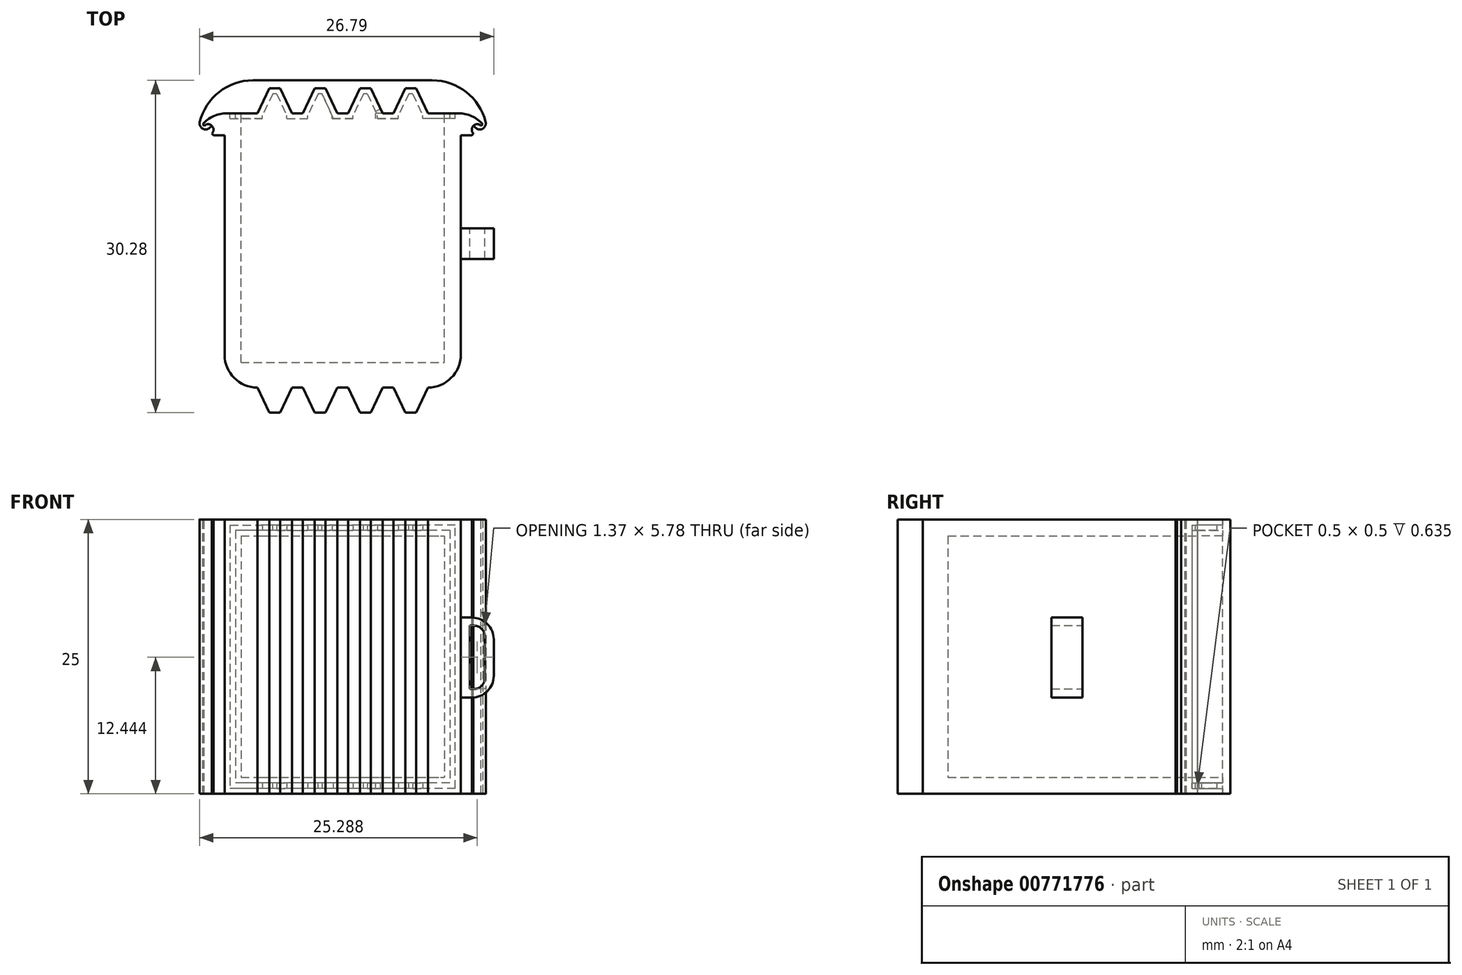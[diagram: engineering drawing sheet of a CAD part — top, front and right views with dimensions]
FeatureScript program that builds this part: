
annotation { "Feature Type Name" : "Feature", "Feature Type Description" : "" }
export const myFeature = defineFeature(function(context is Context, id is Id, definition is map)
    precondition{}
    {
        {
            var Q0;
            Q0=qCreatedBy(makeId("Top.planeOp"),FACE);
            var sketch = newSketch(context, id + "F0", { "sketchPlane" : qUnion([Q0])});
            skLineSegment(sketch, "E0", {"start": v(-21.99, 0) * mm, "end": v(-21.99, 25) * mm});
            skLineSegment(sketch, "E1", {"start": v(-21.99, 25) * mm, "end": v(-18.99, 25) * mm});
            skLineSegment(sketch, "E2", {"start": v(-18.99, 25) * mm, "end": v(-17.92, 27.28) * mm});
            skLineSegment(sketch, "E3", {"start": v(-17.92, 27.28) * mm, "end": v(-16.92, 27.28) * mm});
            skLineSegment(sketch, "E4", {"start": v(-16.92, 27.28) * mm, "end": v(-15.86, 25) * mm});
            skLineSegment(sketch, "E5", {"start": v(-15.86, 25) * mm, "end": v(-14.86, 25) * mm});
            skLineSegment(sketch, "E6", {"start": v(-14.86, 25) * mm, "end": v(-13.8, 27.28) * mm});
            skLineSegment(sketch, "E7", {"start": v(-13.8, 27.28) * mm, "end": v(-12.8, 27.28) * mm});
            skLineSegment(sketch, "E8", {"start": v(-12.8, 27.28) * mm, "end": v(-11.73, 25) * mm});
            skLineSegment(sketch, "E9", {"start": v(-11.73, 25) * mm, "end": v(-10.73, 25) * mm});
            skLineSegment(sketch, "E10", {"start": v(-10.73, 25) * mm, "end": v(-9.67, 27.28) * mm});
            skLineSegment(sketch, "E11", {"start": v(-9.67, 27.28) * mm, "end": v(-8.67, 27.28) * mm});
            skLineSegment(sketch, "E12", {"start": v(-8.67, 27.28) * mm, "end": v(-7.6, 25) * mm});
            skLineSegment(sketch, "E13", {"start": v(-7.6, 25) * mm, "end": v(-6.6, 25) * mm});
            skLineSegment(sketch, "E14", {"start": v(-6.6, 25) * mm, "end": v(-5.54, 27.28) * mm});
            skLineSegment(sketch, "E15", {"start": v(-5.54, 27.28) * mm, "end": v(-4.54, 27.28) * mm});
            skLineSegment(sketch, "E16", {"start": v(-4.54, 27.28) * mm, "end": v(-3.47, 25) * mm});
            skLineSegment(sketch, "E17", {"start": v(-3.47, 25) * mm, "end": v(-0.47, 25) * mm});
            skLineSegment(sketch, "E18", {"start": v(-0.47, 25) * mm, "end": v(-0.47, 0) * mm});
            skLineSegment(sketch, "E19", {"start": v(-33.17, 12.5) * mm, "end": v(42.68, 12.5) * mm, "construction": true});
            skLineSegment(sketch, "E20.MirrorCS", {"start": v(-13.8, -2.28) * mm, "end": v(-12.8, -2.28) * mm});
            skLineSegment(sketch, "E21.MirrorCS", {"start": v(-9.67, -2.28) * mm, "end": v(-8.67, -2.28) * mm});
            skLineSegment(sketch, "E22.MirrorCS", {"start": v(-7.6, 0) * mm, "end": v(-6.6, 0) * mm});
            skLineSegment(sketch, "E23.MirrorCS", {"start": v(-15.86, 0) * mm, "end": v(-14.86, 0) * mm});
            skLineSegment(sketch, "E24.MirrorCS", {"start": v(-5.54, -2.28) * mm, "end": v(-4.54, -2.28) * mm});
            skLineSegment(sketch, "E25.MirrorCS", {"start": v(-21.99, 0) * mm, "end": v(-18.99, 0) * mm});
            skLineSegment(sketch, "E26.MirrorCS", {"start": v(-14.86, 0) * mm, "end": v(-13.8, -2.28) * mm});
            skLineSegment(sketch, "E27.MirrorCS", {"start": v(-4.54, -2.28) * mm, "end": v(-3.47, 0) * mm});
            skLineSegment(sketch, "E28.MirrorCS", {"start": v(-10.73, 0) * mm, "end": v(-9.67, -2.28) * mm});
            skLineSegment(sketch, "E29.MirrorCS", {"start": v(-18.99, 0) * mm, "end": v(-17.92, -2.28) * mm});
            skLineSegment(sketch, "E30.MirrorCS", {"start": v(-11.73, 0) * mm, "end": v(-10.73, 0) * mm});
            skLineSegment(sketch, "E31.MirrorCS", {"start": v(-3.47, 0) * mm, "end": v(-0.47, 0) * mm});
            skLineSegment(sketch, "E32.MirrorCS", {"start": v(-16.92, -2.28) * mm, "end": v(-15.86, 0) * mm});
            skLineSegment(sketch, "E33.MirrorCS", {"start": v(-17.92, -2.28) * mm, "end": v(-16.92, -2.28) * mm});
            skLineSegment(sketch, "E34.MirrorCS", {"start": v(-12.8, -2.28) * mm, "end": v(-11.73, 0) * mm});
            skLineSegment(sketch, "E35.MirrorCS", {"start": v(-6.6, 0) * mm, "end": v(-5.54, -2.28) * mm});
            skLineSegment(sketch, "E36.MirrorCS", {"start": v(-8.67, -2.28) * mm, "end": v(-7.6, 0) * mm});
            skSolve(sketch);
        }
        {
            var Q0;
            Q0=makeQuery(id+"F0.imprint","IMPRINT",FACE,{"disambiguationData":[TD([[makeQuery(id+"F0.imprint","IMPRINT",EDGE,{"derivedFrom":sQuery(id+"F0.wireOp",EDGE,"E0")}),-1.0]])]});
            extrude(context, id + "F1", {"entities" : qUnion([Q0]), "depth" : 25 * mm, "offsetDistance" : 25 * mm});
        }
        {
            var Q0;
            Q0=makeQuery(id+"F1.opExtrude","SWEPT_FACE",FACE,{"disambiguationData":[OSD([sQuery(id+"F0.wireOp",EDGE,"E15")])]});
            var sketch = newSketch(context, id + "F2", { "sketchPlane" : qUnion([Q0])});
            skLineSegment(sketch, "E37.0", {"start": v(20.49, 23.5) * mm, "end": v(20.49, 1.5) * mm});
            skLineSegment(sketch, "E38", {"start": v(20.49, 1.5) * mm, "end": v(1.97, 1.5) * mm});
            skLineSegment(sketch, "E39.0", {"start": v(1.97, 23.5) * mm, "end": v(1.97, 1.5) * mm});
            skLineSegment(sketch, "E40", {"start": v(20.49, 23.5) * mm, "end": v(1.97, 23.5) * mm});
            skPoint(sketch, "E41.start.orphan", {"position": v(24.34, 0) * mm});
            skSolve(sketch);
        }
        {
            var Q0;
            Q0 = qSketchRegion(id + "F2", true);
            extrude(context, id + "F3", {"entities" : qUnion([Q0]), "operationType" : NewBodyOperationType.REMOVE, "oppositeDirection" : true, "depth" : 25 * mm, "offsetDistance" : 25 * mm});
        }
        {
            var Q0;
            Q0=makeQuery(id+"F1.opExtrude","SWEPT_FACE",FACE,{"disambiguationData":[OSD([sQuery(id+"F0.wireOp",EDGE,"E1")])]});
            var sketch = newSketch(context, id + "F4", { "sketchPlane" : qUnion([Q0])});
            skLineSegment(sketch, "E42", {"start": v(-1.53, 0) * mm, "end": v(-1.53, 25) * mm});
            skLineSegment(sketch, "E43", {"start": v(23.99, 0) * mm, "end": v(23.99, 25) * mm});
            skLineSegment(sketch, "E44", {"start": v(23.99, 25) * mm, "end": v(21.99, 25) * mm});
            skLineSegment(sketch, "E45", {"start": v(23.99, 0) * mm, "end": v(21.99, 0) * mm});
            skLineSegment(sketch, "E46.0", {"start": v(0.47, 25) * mm, "end": v(0.47, 0) * mm});
            skLineSegment(sketch, "E47.0", {"start": v(21.99, 25) * mm, "end": v(21.99, 0) * mm});
            skLineSegment(sketch, "E48.trimOffspring", {"start": v(0.47, 0) * mm, "end": v(-1.53, 0) * mm});
            skLineSegment(sketch, "E49.trimOffspring", {"start": v(0.47, 25) * mm, "end": v(-1.53, 25) * mm});
            skSolve(sketch);
        }
        {
            var Q0;
            Q0=makeQuery(id+"F4.imprint","IMPRINT",FACE,{"disambiguationData":[TD([[makeQuery(id+"F4.imprint","IMPRINT",EDGE,{"derivedFrom":sQuery(id+"F4.wireOp",EDGE,"E42")}),-1.0]])]});
            var Q1;
            Q1=makeQuery(id+"F4.imprint","IMPRINT",FACE,{"disambiguationData":[TD([[makeQuery(id+"F4.imprint","IMPRINT",EDGE,{"derivedFrom":sQuery(id+"F4.wireOp",EDGE,"E43")}),1.0]])]});
            extrude(context, id + "F5", {"entities" : qUnion([Q0, Q1]), "operationType" : NewBodyOperationType.ADD, "oppositeDirection" : true, "depth" : 2 * mm, "offsetDistance" : 25 * mm});
        }
        {
            var Q0;
            Q0=makeQuery(id+"F5.opExtrude","CAP_EDGE",EDGE,{"disambiguationData":[OSD([sQuery(id+"F4.wireOp",EDGE,"E42")])],"isStart":false});
            var Q1;
            Q1=makeQuery(id+"F5.opExtrude","CAP_EDGE",EDGE,{"disambiguationData":[OSD([sQuery(id+"F4.wireOp",EDGE,"E43")])],"isStart":false});
            chamfer(context, id + "F6", {"entities" : qUnion([Q0, Q1]), "width" : 1 * mm, "tangentPropagation" : true});
        }
        {
            var Q0;
            Q0=makeQuery(id+"F5.boolean.opBoolean","MERGE",FACE,{"derivedFrom":[makeQuery(id+"F1.opExtrude","CAP_FACE",FACE,{"disambiguationData":[OSD([sQuery(id+"F0.wireOp",EDGE,"E0"),sQuery(id+"F0.wireOp",EDGE,"E1"),sQuery(id+"F0.wireOp",EDGE,"E2"),sQuery(id+"F0.wireOp",EDGE,"E3"),sQuery(id+"F0.wireOp",EDGE,"E4"),sQuery(id+"F0.wireOp",EDGE,"E5"),sQuery(id+"F0.wireOp",EDGE,"E6"),sQuery(id+"F0.wireOp",EDGE,"E7"),sQuery(id+"F0.wireOp",EDGE,"E8"),sQuery(id+"F0.wireOp",EDGE,"E9"),sQuery(id+"F0.wireOp",EDGE,"E10"),sQuery(id+"F0.wireOp",EDGE,"E11"),sQuery(id+"F0.wireOp",EDGE,"E12"),sQuery(id+"F0.wireOp",EDGE,"E13"),sQuery(id+"F0.wireOp",EDGE,"E14"),sQuery(id+"F0.wireOp",EDGE,"E15"),sQuery(id+"F0.wireOp",EDGE,"E16"),sQuery(id+"F0.wireOp",EDGE,"E17"),sQuery(id+"F0.wireOp",EDGE,"E18"),sQuery(id+"F0.wireOp",EDGE,"E20.MirrorCS"),sQuery(id+"F0.wireOp",EDGE,"E21.MirrorCS"),sQuery(id+"F0.wireOp",EDGE,"E22.MirrorCS"),sQuery(id+"F0.wireOp",EDGE,"E23.MirrorCS"),sQuery(id+"F0.wireOp",EDGE,"E24.MirrorCS"),sQuery(id+"F0.wireOp",EDGE,"E25.MirrorCS"),sQuery(id+"F0.wireOp",EDGE,"E26.MirrorCS"),sQuery(id+"F0.wireOp",EDGE,"E27.MirrorCS"),sQuery(id+"F0.wireOp",EDGE,"E28.MirrorCS"),sQuery(id+"F0.wireOp",EDGE,"E29.MirrorCS"),sQuery(id+"F0.wireOp",EDGE,"E30.MirrorCS"),sQuery(id+"F0.wireOp",EDGE,"E31.MirrorCS"),sQuery(id+"F0.wireOp",EDGE,"E32.MirrorCS"),sQuery(id+"F0.wireOp",EDGE,"E33.MirrorCS"),sQuery(id+"F0.wireOp",EDGE,"E34.MirrorCS"),sQuery(id+"F0.wireOp",EDGE,"E35.MirrorCS"),sQuery(id+"F0.wireOp",EDGE,"E36.MirrorCS")])],"isStart":false}),makeQuery(id+"F5.opExtrude","SWEPT_FACE",FACE,{"disambiguationData":[OSD([sQuery(id+"F4.wireOp",EDGE,"E44")])]}),makeQuery(id+"F5.opExtrude","SWEPT_FACE",FACE,{"disambiguationData":[OSD([sQuery(id+"F4.wireOp",EDGE,"E49.trimOffspring")])]})]});
            var sketch = newSketch(context, id + "F7", { "sketchPlane" : qUnion([Q0])});
            skCircle(sketch, "E50", {"center": v(1.03, 23.5) * mm, "radius": 0.5 * mm});
            skPoint(sketch, "E51.startSnap0", {"position": v(-11.23, 25) * mm});
            skCircle(sketch, "E52.MirrorC", {"center": v(-23.49, 23.5) * mm, "radius": 0.5 * mm});
            skSolve(sketch);
        }
        {
            var Q0;
            Q0 = qSketchRegion(id + "F7", true);
            extrude(context, id + "F8", {"entities" : qUnion([Q0]), "operationType" : NewBodyOperationType.REMOVE, "oppositeDirection" : true, "depth" : 25 * mm, "offsetDistance" : 25 * mm});
        }
        {
            var Q0;
            Q0=makeQuery(id+"F5.opExtrude","CAP_EDGE",EDGE,{"disambiguationData":[OSD([sQuery(id+"F4.wireOp",EDGE,"E43")])],"isStart":true});
            var Q1;
            Q1=makeQuery(id+"F5.opExtrude","CAP_EDGE",EDGE,{"disambiguationData":[OSD([sQuery(id+"F4.wireOp",EDGE,"E42")])],"isStart":true});
            fillet(context, id + "F9", {"entities" : qUnion([Q0, Q1]), "radius" : 3 * mm, "tangentPropagation" : true, "allowEdgeOverflow" : false});
        }
        {
            var Q0;
            {var subQ0=makeQuery(id+"F3.opExtrude","SWEPT_FACE",FACE,{"disambiguationData":[OSD([sQuery(id+"F2.wireOp",EDGE,"E40")])]});var subQ1=sQuery(id+"F0.wireOp",EDGE,"E6");var subQ2=makeQuery(id+"F1.opExtrude","SWEPT_FACE",FACE,{"disambiguationData":[OSD([subQ1])]});var subQ4=sQuery(id+"F0.wireOp",EDGE,"E7");Q0=makeQuery(id+"FOoDHxv8LMfWURN_1.boolean.opBoolean","SPLIT",FACE,{"disambiguationData":[TD([subQ2])],"derivedFrom":makeQuery(id+"F3.boolean.opBoolean","SPLIT",FACE,{"disambiguationData":[TD([subQ0])],"derivedFrom":makeQuery(id+"F1.opExtrude","SWEPT_FACE",FACE,{"disambiguationData":[OSD([subQ4])]})})});}
            var sketch = newSketch(context, id + "F10", { "sketchPlane" : qUnion([Q0])});
            skLineSegment(sketch, "E53.0", {"start": v(1.47, 24) * mm, "end": v(1.47, 1) * mm});
            skLineSegment(sketch, "E54", {"start": v(0.97, 24.5) * mm, "end": v(0.97, 0.5) * mm});
            skLineSegment(sketch, "E55", {"start": v(-13.27, 12.5) * mm, "end": v(32.52, 12.5) * mm, "construction": true});
            skLineSegment(sketch, "E56", {"start": v(0.97, 24.5) * mm, "end": v(21.49, 24.5) * mm});
            skLineSegment(sketch, "E57", {"start": v(1.47, 24) * mm, "end": v(20.99, 24) * mm});
            skLineSegment(sketch, "E58.MirrorCS", {"start": v(0.97, 0.5) * mm, "end": v(21.49, 0.5) * mm});
            skLineSegment(sketch, "E59.MirrorCS", {"start": v(1.47, 1) * mm, "end": v(20.99, 1) * mm});
            skLineSegment(sketch, "E60.MirrorCS", {"start": v(0.97, 0.5) * mm, "end": v(0.97, 24.5) * mm});
            skLineSegment(sketch, "E61", {"start": v(11.23, 28.79) * mm, "end": v(11.23, -9.21) * mm, "construction": true});
            skLineSegment(sketch, "E62.MirrorCS", {"start": v(20.99, 1) * mm, "end": v(20.99, 24) * mm});
            skLineSegment(sketch, "E63.MirrorCS", {"start": v(21.49, 0.5) * mm, "end": v(21.49, 24.5) * mm});
            skPoint(sketch, "E64.orphan", {"position": v(22.44, 24.5) * mm});
            skPoint(sketch, "E65.orphan", {"position": v(21.49, 30) * mm});
            skPoint(sketch, "E66.orphan", {"position": v(22.46, 24) * mm});
            skPoint(sketch, "E67.orphan", {"position": v(0.97, 30) * mm});
            skPoint(sketch, "E68.orphan", {"position": v(0.97, -5) * mm});
            skPoint(sketch, "E69.trimOffspring.end.orphan", {"position": v(22.46, 1) * mm});
            skPoint(sketch, "E70.orphan", {"position": v(22.44, 0.5) * mm});
            skSolve(sketch);
        }
        {
            var Q0;
            {var subQ13=sQuery(id+"F10.wireOp",EDGE,"E53.0");Q0=makeQuery(id+"F10.imprint","IMPRINT",FACE,{"disambiguationData":[TD([[makeQuery(id+"F10.imprint","IMPRINT",EDGE,{"derivedFrom":subQ13}),-1.0]])]});}
            extrude(context, id + "F11", {"entities" : qUnion([Q0]), "operationType" : NewBodyOperationType.REMOVE, "oppositeDirection" : true, "depth" : 0.5 * mm, "offsetDistance" : 25 * mm});
        }
        {
            var Q0;
            {var subQ1=sQuery(id+"F0.wireOp",EDGE,"E16");Q0=makeQuery(id+"F3.boolean.opBoolean","SPLIT",FACE,{"disambiguationData":[TD([makeQuery(id+"F3.opExtrude","SWEPT_FACE",FACE,{"disambiguationData":[OSD([sQuery(id+"F2.wireOp",EDGE,"E38")])]})])],"derivedFrom":makeQuery(id+"F1.opExtrude","SWEPT_FACE",FACE,{"disambiguationData":[OSD([subQ1])]})});}
            var sketch = newSketch(context, id + "F12", { "sketchPlane" : qUnion([Q0])});
            skLineSegment(sketch, "E71", {"start": v(24.13, 0.5) * mm, "end": v(24.13, 1) * mm});
            skLineSegment(sketch, "E72", {"start": v(26.64, 1) * mm, "end": v(24.13, 1) * mm});
            skLineSegment(sketch, "E73", {"start": v(26.64, 0.5) * mm, "end": v(24.13, 0.5) * mm});
            skLineSegment(sketch, "E74", {"start": v(26.64, 0.5) * mm, "end": v(26.64, 1) * mm});
            skSolve(sketch);
        }
        {
            var Q0;
            {var subQ0=sQuery(id+"F12.wireOp",EDGE,"E71");Q0=makeQuery(id+"F12.imprint","IMPRINT",FACE,{"disambiguationData":[TD([[makeQuery(id+"F12.imprint","IMPRINT",EDGE,{"derivedFrom":subQ0}),1.0]])]});}
            var Q1;
            {var subQ0=sQuery(id+"F12.wireOp",EDGE,"E74");Q1=makeQuery(id+"F12.imprint","IMPRINT",FACE,{"disambiguationData":[TD([[makeQuery(id+"F12.imprint","IMPRINT",EDGE,{"derivedFrom":subQ0}),1.0]])]});}
            extrude(context, id + "F13", {"entities" : qUnion([Q0, Q1]), "operationType" : NewBodyOperationType.REMOVE, "oppositeDirection" : true, "depth" : 0.5 * mm, "offsetDistance" : 25 * mm});
        }
        {
            var Q0;
            {var subQ1=sQuery(id+"F0.wireOp",EDGE,"E12");Q0=makeQuery(id+"F3.boolean.opBoolean","SPLIT",FACE,{"disambiguationData":[TD([makeQuery(id+"F3.opExtrude","SWEPT_FACE",FACE,{"disambiguationData":[OSD([sQuery(id+"F2.wireOp",EDGE,"E38")])]})])],"derivedFrom":makeQuery(id+"F1.opExtrude","SWEPT_FACE",FACE,{"disambiguationData":[OSD([subQ1])]})});}
            var sketch = newSketch(context, id + "F14", { "sketchPlane" : qUnion([Q0])});
            skLineSegment(sketch, "E75", {"start": v(26.3, 0.5) * mm, "end": v(26.3, 1) * mm});
            skLineSegment(sketch, "E76", {"start": v(28.82, 1) * mm, "end": v(26.3, 1) * mm});
            skLineSegment(sketch, "E77", {"start": v(28.82, 0.5) * mm, "end": v(26.3, 0.5) * mm});
            skLineSegment(sketch, "E78", {"start": v(28.82, 0.5) * mm, "end": v(28.82, 1) * mm});
            skSolve(sketch);
        }
        {
            var Q0;
            Q0 = qSketchRegion(id + "F14", true);
            extrude(context, id + "F15", {"entities" : qUnion([Q0]), "operationType" : NewBodyOperationType.REMOVE, "oppositeDirection" : true, "depth" : 0.5 * mm, "offsetDistance" : 25 * mm});
        }
        {
            var Q0;
            {var subQ1=sQuery(id+"F0.wireOp",EDGE,"E8");Q0=makeQuery(id+"F3.boolean.opBoolean","SPLIT",FACE,{"disambiguationData":[TD([makeQuery(id+"F3.opExtrude","SWEPT_FACE",FACE,{"disambiguationData":[OSD([sQuery(id+"F2.wireOp",EDGE,"E38")])]})])],"derivedFrom":makeQuery(id+"F1.opExtrude","SWEPT_FACE",FACE,{"disambiguationData":[OSD([subQ1])]})});}
            var sketch = newSketch(context, id + "F16", { "sketchPlane" : qUnion([Q0])});
            skLineSegment(sketch, "E79", {"start": v(27.3, 0.5) * mm, "end": v(27.3, 1) * mm});
            skLineSegment(sketch, "E80", {"start": v(29.82, 1) * mm, "end": v(27.3, 1) * mm});
            skLineSegment(sketch, "E81", {"start": v(29.82, 0.5) * mm, "end": v(27.3, 0.5) * mm});
            skLineSegment(sketch, "E82", {"start": v(29.82, 0.5) * mm, "end": v(29.82, 1) * mm});
            skSolve(sketch);
        }
        {
            var Q0;
            Q0 = qSketchRegion(id + "F16", true);
            extrude(context, id + "F17", {"entities" : qUnion([Q0]), "operationType" : NewBodyOperationType.REMOVE, "oppositeDirection" : true, "depth" : 0.5 * mm, "offsetDistance" : 25 * mm});
        }
        {
            var Q0;
            {var subQ1=sQuery(id+"F0.wireOp",EDGE,"E4");Q0=makeQuery(id+"F3.boolean.opBoolean","SPLIT",FACE,{"disambiguationData":[TD([makeQuery(id+"F3.opExtrude","SWEPT_FACE",FACE,{"disambiguationData":[OSD([sQuery(id+"F2.wireOp",EDGE,"E38")])]})])],"derivedFrom":makeQuery(id+"F1.opExtrude","SWEPT_FACE",FACE,{"disambiguationData":[OSD([subQ1])]})});}
            var sketch = newSketch(context, id + "F18", { "sketchPlane" : qUnion([Q0])});
            skLineSegment(sketch, "E83", {"start": v(29.36, 0.5) * mm, "end": v(29.36, 1) * mm});
            skLineSegment(sketch, "E84", {"start": v(31.88, 1) * mm, "end": v(29.36, 1) * mm});
            skLineSegment(sketch, "E85", {"start": v(31.88, 0.5) * mm, "end": v(29.36, 0.5) * mm});
            skLineSegment(sketch, "E86", {"start": v(31.88, 0.5) * mm, "end": v(31.88, 1) * mm});
            skSolve(sketch);
        }
        {
            var Q0;
            Q0 = qSketchRegion(id + "F18", true);
            extrude(context, id + "F19", {"entities" : qUnion([Q0]), "operationType" : NewBodyOperationType.REMOVE, "oppositeDirection" : true, "depth" : 0.5 * mm, "offsetDistance" : 25 * mm});
        }
        {
            var Q0;
            {var subQ1=sQuery(id+"F0.wireOp",EDGE,"E16");Q0=makeQuery(id+"F3.boolean.opBoolean","SPLIT",FACE,{"disambiguationData":[TD([makeQuery(id+"F3.opExtrude","SWEPT_FACE",FACE,{"disambiguationData":[OSD([sQuery(id+"F2.wireOp",EDGE,"E40")])]})])],"derivedFrom":makeQuery(id+"F1.opExtrude","SWEPT_FACE",FACE,{"disambiguationData":[OSD([subQ1])]})});}
            var sketch = newSketch(context, id + "F20", { "sketchPlane" : qUnion([Q0])});
            skLineSegment(sketch, "E87", {"start": v(24.13, 24) * mm, "end": v(24.13, 24.5) * mm});
            skLineSegment(sketch, "E88", {"start": v(26.64, 24.5) * mm, "end": v(24.13, 24.5) * mm});
            skLineSegment(sketch, "E89", {"start": v(26.64, 24) * mm, "end": v(24.13, 24) * mm});
            skLineSegment(sketch, "E90", {"start": v(26.64, 24) * mm, "end": v(26.64, 24.5) * mm});
            skSolve(sketch);
        }
        {
            var Q0;
            {var subQ1=sQuery(id+"F0.wireOp",EDGE,"E12");Q0=makeQuery(id+"F3.boolean.opBoolean","SPLIT",FACE,{"disambiguationData":[TD([makeQuery(id+"F3.opExtrude","SWEPT_FACE",FACE,{"disambiguationData":[OSD([sQuery(id+"F2.wireOp",EDGE,"E40")])]})])],"derivedFrom":makeQuery(id+"F1.opExtrude","SWEPT_FACE",FACE,{"disambiguationData":[OSD([subQ1])]})});}
            var sketch = newSketch(context, id + "F21", { "sketchPlane" : qUnion([Q0])});
            skLineSegment(sketch, "E91", {"start": v(25.87, 24) * mm, "end": v(25.87, 24.5) * mm});
            skLineSegment(sketch, "E92", {"start": v(28.39, 24.5) * mm, "end": v(25.87, 24.5) * mm});
            skLineSegment(sketch, "E93", {"start": v(28.39, 24) * mm, "end": v(25.87, 24) * mm});
            skLineSegment(sketch, "E94", {"start": v(28.39, 24) * mm, "end": v(28.39, 24.5) * mm});
            skSolve(sketch);
        }
        {
            var Q0;
            {var subQ1=sQuery(id+"F0.wireOp",EDGE,"E8");Q0=makeQuery(id+"F3.boolean.opBoolean","SPLIT",FACE,{"disambiguationData":[TD([makeQuery(id+"F3.opExtrude","SWEPT_FACE",FACE,{"disambiguationData":[OSD([sQuery(id+"F2.wireOp",EDGE,"E40")])]})])],"derivedFrom":makeQuery(id+"F1.opExtrude","SWEPT_FACE",FACE,{"disambiguationData":[OSD([subQ1])]})});}
            var sketch = newSketch(context, id + "F22", { "sketchPlane" : qUnion([Q0])});
            skLineSegment(sketch, "E95", {"start": v(27.62, 24) * mm, "end": v(27.62, 24.5) * mm});
            skLineSegment(sketch, "E96", {"start": v(30.13, 24.5) * mm, "end": v(27.62, 24.5) * mm});
            skLineSegment(sketch, "E97", {"start": v(30.13, 24) * mm, "end": v(27.62, 24) * mm});
            skLineSegment(sketch, "E98", {"start": v(30.13, 24) * mm, "end": v(30.13, 24.5) * mm});
            skSolve(sketch);
        }
        {
            var Q0;
            {var subQ1=sQuery(id+"F0.wireOp",EDGE,"E4");Q0=makeQuery(id+"F3.boolean.opBoolean","SPLIT",FACE,{"disambiguationData":[TD([makeQuery(id+"F3.opExtrude","SWEPT_FACE",FACE,{"disambiguationData":[OSD([sQuery(id+"F2.wireOp",EDGE,"E40")])]})])],"derivedFrom":makeQuery(id+"F1.opExtrude","SWEPT_FACE",FACE,{"disambiguationData":[OSD([subQ1])]})});}
            var sketch = newSketch(context, id + "F23", { "sketchPlane" : qUnion([Q0])});
            skLineSegment(sketch, "E99", {"start": v(29.36, 24) * mm, "end": v(29.36, 24.5) * mm});
            skLineSegment(sketch, "E100", {"start": v(31.88, 24.5) * mm, "end": v(29.36, 24.5) * mm});
            skLineSegment(sketch, "E101", {"start": v(31.88, 24) * mm, "end": v(29.36, 24) * mm});
            skLineSegment(sketch, "E102", {"start": v(31.88, 24) * mm, "end": v(31.88, 24.5) * mm});
            skSolve(sketch);
        }
        {
            var Q0;
            Q0 = qSketchRegion(id + "F20", true);
            var Q1;
            Q1 = qSketchRegion(id + "F21", true);
            var Q2;
            Q2 = qSketchRegion(id + "F22", true);
            var Q3;
            Q3 = qSketchRegion(id + "F23", true);
            extrude(context, id + "F24", {"entities" : qUnion([Q0, Q1, Q2, Q3]), "operationType" : NewBodyOperationType.REMOVE, "oppositeDirection" : true, "depth" : 0.5 * mm, "offsetDistance" : 25 * mm});
        }
        {
            var Q0;
            {var subQ1=sQuery(id+"F0.wireOp",EDGE,"E7");Q0=makeQuery(id+"F3.boolean.opBoolean","SPLIT",FACE,{"disambiguationData":[TD([makeQuery(id+"F3.opExtrude","SWEPT_FACE",FACE,{"disambiguationData":[OSD([sQuery(id+"F2.wireOp",EDGE,"E40")])]})])],"derivedFrom":makeQuery(id+"F1.opExtrude","SWEPT_FACE",FACE,{"disambiguationData":[OSD([subQ1])]})});}
            var sketch = newSketch(context, id + "F25", { "sketchPlane" : qUnion([Q0])});
            skLineSegment(sketch, "E103.bottom", {"start": v(13.8, 24.5) * mm, "end": v(12.8, 24.5) * mm});
            skLineSegment(sketch, "E103.top", {"start": v(13.8, 24) * mm, "end": v(12.8, 24) * mm});
            skLineSegment(sketch, "E103.left", {"start": v(13.8, 24.5) * mm, "end": v(13.8, 24) * mm});
            skLineSegment(sketch, "E103.right", {"start": v(12.8, 24.5) * mm, "end": v(12.8, 24) * mm});
            skSolve(sketch);
        }
        {
            var Q0;
            Q0=makeQuery(id+"F25.imprint","IMPRINT",FACE,{"disambiguationData":[TD([[makeQuery(id+"F25.imprint","IMPRINT",EDGE,{"derivedFrom":sQuery(id+"F25.wireOp",EDGE,"E103.bottom")}),1.0]])]});
            extrude(context, id + "F26", {"entities" : qUnion([Q0]), "operationType" : NewBodyOperationType.REMOVE, "oppositeDirection" : true, "depth" : 0.5 * mm, "offsetDistance" : 25 * mm});
        }
        {
            var Q0;
            {var subQ1=sQuery(id+"F0.wireOp",EDGE,"E14");Q0=makeQuery(id+"F3.boolean.opBoolean","SPLIT",FACE,{"disambiguationData":[TD([makeQuery(id+"F3.opExtrude","SWEPT_FACE",FACE,{"disambiguationData":[OSD([sQuery(id+"F2.wireOp",EDGE,"E38")])]})])],"derivedFrom":makeQuery(id+"F1.opExtrude","SWEPT_FACE",FACE,{"disambiguationData":[OSD([subQ1])]})});}
            var sketch = newSketch(context, id + "F27", { "sketchPlane" : qUnion([Q0])});
            skLineSegment(sketch, "E104.bottom", {"start": v(-22.39, 0.5) * mm, "end": v(-19.87, 0.5) * mm});
            skLineSegment(sketch, "E104.top", {"start": v(-22.39, 1) * mm, "end": v(-19.87, 1) * mm});
            skLineSegment(sketch, "E104.left", {"start": v(-22.39, 0.5) * mm, "end": v(-22.39, 1) * mm});
            skLineSegment(sketch, "E104.right", {"start": v(-19.87, 0.5) * mm, "end": v(-19.87, 1) * mm});
            skSolve(sketch);
        }
        {
            var Q0;
            {var subQ1=sQuery(id+"F0.wireOp",EDGE,"E10");Q0=makeQuery(id+"F3.boolean.opBoolean","SPLIT",FACE,{"disambiguationData":[TD([makeQuery(id+"F3.opExtrude","SWEPT_FACE",FACE,{"disambiguationData":[OSD([sQuery(id+"F2.wireOp",EDGE,"E38")])]})])],"derivedFrom":makeQuery(id+"F1.opExtrude","SWEPT_FACE",FACE,{"disambiguationData":[OSD([subQ1])]})});}
            var sketch = newSketch(context, id + "F28", { "sketchPlane" : qUnion([Q0])});
            skLineSegment(sketch, "E105.bottom", {"start": v(-21.36, 0.5) * mm, "end": v(-18.12, 0.5) * mm});
            skLineSegment(sketch, "E105.top", {"start": v(-21.36, 1) * mm, "end": v(-18.12, 1) * mm});
            skLineSegment(sketch, "E105.left", {"start": v(-21.36, 0.5) * mm, "end": v(-21.36, 1) * mm});
            skLineSegment(sketch, "E105.right", {"start": v(-18.12, 0.5) * mm, "end": v(-18.12, 1) * mm});
            skSolve(sketch);
        }
        {
            var Q0;
            {var subQ1=sQuery(id+"F0.wireOp",EDGE,"E6");Q0=makeQuery(id+"F3.boolean.opBoolean","SPLIT",FACE,{"disambiguationData":[TD([makeQuery(id+"F3.opExtrude","SWEPT_FACE",FACE,{"disambiguationData":[OSD([sQuery(id+"F2.wireOp",EDGE,"E38")])]})])],"derivedFrom":makeQuery(id+"F1.opExtrude","SWEPT_FACE",FACE,{"disambiguationData":[OSD([subQ1])]})});}
            var sketch = newSketch(context, id + "F29", { "sketchPlane" : qUnion([Q0])});
            skLineSegment(sketch, "E106.bottom", {"start": v(-18.9, 0.5) * mm, "end": v(-16.38, 0.5) * mm});
            skLineSegment(sketch, "E106.top", {"start": v(-18.9, 1) * mm, "end": v(-16.38, 1) * mm});
            skLineSegment(sketch, "E106.left", {"start": v(-18.9, 0.5) * mm, "end": v(-18.9, 1) * mm});
            skLineSegment(sketch, "E106.right", {"start": v(-16.38, 0.5) * mm, "end": v(-16.38, 1) * mm});
            skSolve(sketch);
        }
        {
            var Q0;
            {var subQ1=sQuery(id+"F0.wireOp",EDGE,"E2");Q0=makeQuery(id+"F3.boolean.opBoolean","SPLIT",FACE,{"disambiguationData":[TD([makeQuery(id+"F3.opExtrude","SWEPT_FACE",FACE,{"disambiguationData":[OSD([sQuery(id+"F2.wireOp",EDGE,"E38")])]})])],"derivedFrom":makeQuery(id+"F1.opExtrude","SWEPT_FACE",FACE,{"disambiguationData":[OSD([subQ1])]})});}
            var sketch = newSketch(context, id + "F30", { "sketchPlane" : qUnion([Q0])});
            skLineSegment(sketch, "E107.bottom", {"start": v(-17.15, 0.5) * mm, "end": v(-14.63, 0.5) * mm});
            skLineSegment(sketch, "E107.top", {"start": v(-17.15, 1) * mm, "end": v(-14.63, 1) * mm});
            skLineSegment(sketch, "E107.left", {"start": v(-17.15, 0.5) * mm, "end": v(-17.15, 1) * mm});
            skLineSegment(sketch, "E107.right", {"start": v(-14.63, 0.5) * mm, "end": v(-14.63, 1) * mm});
            skSolve(sketch);
        }
        {
            var Q0;
            {var subQ1=sQuery(id+"F0.wireOp",EDGE,"E2");Q0=makeQuery(id+"F3.boolean.opBoolean","SPLIT",FACE,{"disambiguationData":[TD([makeQuery(id+"F3.opExtrude","SWEPT_FACE",FACE,{"disambiguationData":[OSD([sQuery(id+"F2.wireOp",EDGE,"E40")])]})])],"derivedFrom":makeQuery(id+"F1.opExtrude","SWEPT_FACE",FACE,{"disambiguationData":[OSD([subQ1])]})});}
            var sketch = newSketch(context, id + "F31", { "sketchPlane" : qUnion([Q0])});
            skLineSegment(sketch, "E108.bottom", {"start": v(-17.15, 24) * mm, "end": v(-14.63, 24) * mm});
            skLineSegment(sketch, "E108.top", {"start": v(-17.15, 24.5) * mm, "end": v(-14.63, 24.5) * mm});
            skLineSegment(sketch, "E108.left", {"start": v(-17.15, 24) * mm, "end": v(-17.15, 24.5) * mm});
            skLineSegment(sketch, "E108.right", {"start": v(-14.63, 24) * mm, "end": v(-14.63, 24.5) * mm});
            skSolve(sketch);
        }
        {
            var Q0;
            {var subQ1=sQuery(id+"F0.wireOp",EDGE,"E6");Q0=makeQuery(id+"F3.boolean.opBoolean","SPLIT",FACE,{"disambiguationData":[TD([makeQuery(id+"F3.opExtrude","SWEPT_FACE",FACE,{"disambiguationData":[OSD([sQuery(id+"F2.wireOp",EDGE,"E40")])]})])],"derivedFrom":makeQuery(id+"F1.opExtrude","SWEPT_FACE",FACE,{"disambiguationData":[OSD([subQ1])]})});}
            var sketch = newSketch(context, id + "F32", { "sketchPlane" : qUnion([Q0])});
            skLineSegment(sketch, "E109.bottom", {"start": v(-18.9, 24) * mm, "end": v(-16.38, 24) * mm});
            skLineSegment(sketch, "E109.top", {"start": v(-18.9, 24.5) * mm, "end": v(-16.38, 24.5) * mm});
            skLineSegment(sketch, "E109.left", {"start": v(-18.9, 24) * mm, "end": v(-18.9, 24.5) * mm});
            skLineSegment(sketch, "E109.right", {"start": v(-16.38, 24) * mm, "end": v(-16.38, 24.5) * mm});
            skSolve(sketch);
        }
        {
            var Q0;
            {var subQ1=sQuery(id+"F0.wireOp",EDGE,"E10");Q0=makeQuery(id+"F3.boolean.opBoolean","SPLIT",FACE,{"disambiguationData":[TD([makeQuery(id+"F3.opExtrude","SWEPT_FACE",FACE,{"disambiguationData":[OSD([sQuery(id+"F2.wireOp",EDGE,"E40")])]})])],"derivedFrom":makeQuery(id+"F1.opExtrude","SWEPT_FACE",FACE,{"disambiguationData":[OSD([subQ1])]})});}
            var sketch = newSketch(context, id + "F33", { "sketchPlane" : qUnion([Q0])});
            skLineSegment(sketch, "E110.bottom", {"start": v(-20.64, 24) * mm, "end": v(-18.12, 24) * mm});
            skLineSegment(sketch, "E110.top", {"start": v(-20.64, 24.5) * mm, "end": v(-18.12, 24.5) * mm});
            skLineSegment(sketch, "E110.left", {"start": v(-20.64, 24) * mm, "end": v(-20.64, 24.5) * mm});
            skLineSegment(sketch, "E110.right", {"start": v(-18.12, 24) * mm, "end": v(-18.12, 24.5) * mm});
            skSolve(sketch);
        }
        {
            var Q0;
            {var subQ1=sQuery(id+"F0.wireOp",EDGE,"E14");Q0=makeQuery(id+"F3.boolean.opBoolean","SPLIT",FACE,{"disambiguationData":[TD([makeQuery(id+"F3.opExtrude","SWEPT_FACE",FACE,{"disambiguationData":[OSD([sQuery(id+"F2.wireOp",EDGE,"E40")])]})])],"derivedFrom":makeQuery(id+"F1.opExtrude","SWEPT_FACE",FACE,{"disambiguationData":[OSD([subQ1])]})});}
            var sketch = newSketch(context, id + "F34", { "sketchPlane" : qUnion([Q0])});
            skLineSegment(sketch, "E111.bottom", {"start": v(-22.39, 24) * mm, "end": v(-19.87, 24) * mm});
            skLineSegment(sketch, "E111.top", {"start": v(-22.39, 24.5) * mm, "end": v(-19.87, 24.5) * mm});
            skLineSegment(sketch, "E111.left", {"start": v(-22.39, 24) * mm, "end": v(-22.39, 24.5) * mm});
            skLineSegment(sketch, "E111.right", {"start": v(-19.87, 24) * mm, "end": v(-19.87, 24.5) * mm});
            skSolve(sketch);
        }
        {
            var Q0;
            Q0 = qSketchRegion(id + "F27", true);
            var Q1;
            Q1 = qSketchRegion(id + "F28", true);
            var Q2;
            Q2 = qSketchRegion(id + "F29", true);
            var Q3;
            Q3 = qSketchRegion(id + "F30", true);
            var Q4;
            Q4 = qSketchRegion(id + "F31", true);
            var Q5;
            Q5 = qSketchRegion(id + "F32", true);
            var Q6;
            Q6 = qSketchRegion(id + "F33", true);
            var Q7;
            Q7 = qSketchRegion(id + "F34", true);
            extrude(context, id + "F35", {"entities" : qUnion([Q0, Q1, Q2, Q3, Q4, Q5, Q6, Q7]), "operationType" : NewBodyOperationType.REMOVE, "oppositeDirection" : true, "depth" : 0.5 * mm, "offsetDistance" : 25 * mm});
        }
        {
            var Q0;
            Q0=makeQuery(id+"F5.boolean.opBoolean","MERGE",FACE,{"derivedFrom":[makeQuery(id+"F1.opExtrude","SWEPT_FACE",FACE,{"disambiguationData":[OSD([sQuery(id+"F0.wireOp",EDGE,"E17")])]}),makeQuery(id+"F5.opExtrude","CAP_FACE",FACE,{"disambiguationData":[OSD([sQuery(id+"F4.wireOp",EDGE,"E42"),sQuery(id+"F4.wireOp",EDGE,"E46.0"),sQuery(id+"F4.wireOp",EDGE,"E48.trimOffspring"),sQuery(id+"F4.wireOp",EDGE,"E49.trimOffspring")])],"isStart":true})]});
            var sketch = newSketch(context, id + "F36", { "sketchPlane" : qUnion([Q0])});
            skLineSegment(sketch, "E112.0", {"start": v(1.47, 24) * mm, "end": v(1.47, 1) * mm});
            skPoint(sketch, "E113.0", {"position": v(18.99, 0.75) * mm});
            skLineSegment(sketch, "E114.0", {"start": v(20.99, 24) * mm, "end": v(20.99, 1) * mm});
            skLineSegment(sketch, "E115.0", {"start": v(21.49, 24.5) * mm, "end": v(21.49, 0.5) * mm});
            skLineSegment(sketch, "E116.0", {"start": v(18.53, 1) * mm, "end": v(18.53, 0.5) * mm});
            skLineSegment(sketch, "E117", {"start": v(18.53, 0.5) * mm, "end": v(21.49, 0.5) * mm});
            skLineSegment(sketch, "E118", {"start": v(18.53, 1) * mm, "end": v(20.99, 1) * mm});
            skLineSegment(sketch, "E119.0", {"start": v(14.4, 1) * mm, "end": v(14.4, 0.5) * mm});
            skLineSegment(sketch, "E120.0", {"start": v(16.31, 1) * mm, "end": v(16.31, 0.5) * mm});
            skLineSegment(sketch, "E121.0", {"start": v(10.28, 1) * mm, "end": v(10.28, 0.5) * mm});
            skLineSegment(sketch, "E122.0", {"start": v(12.05, 0.5) * mm, "end": v(12.05, 1) * mm});
            skLineSegment(sketch, "E123.0", {"start": v(6.15, 1) * mm, "end": v(6.15, 0.5) * mm});
            skLineSegment(sketch, "E124.0", {"start": v(8.24, 0.5) * mm, "end": v(8.24, 1) * mm});
            skLineSegment(sketch, "E125.0", {"start": v(6.15, 24.5) * mm, "end": v(6.15, 24) * mm});
            skLineSegment(sketch, "E126.0", {"start": v(8.05, 24.5) * mm, "end": v(8.05, 24) * mm});
            skLineSegment(sketch, "E127.0", {"start": v(10.28, 24.5) * mm, "end": v(10.28, 24) * mm});
            skLineSegment(sketch, "E128.0", {"start": v(12.18, 24.5) * mm, "end": v(12.18, 24) * mm});
            skLineSegment(sketch, "E129.0", {"start": v(14.4, 24.5) * mm, "end": v(14.4, 24) * mm});
            skLineSegment(sketch, "E130.0", {"start": v(16.31, 24.5) * mm, "end": v(16.31, 24) * mm});
            skLineSegment(sketch, "E131.0", {"start": v(18.53, 24.5) * mm, "end": v(18.53, 24) * mm});
            skLineSegment(sketch, "E132", {"start": v(18.53, 24) * mm, "end": v(20.99, 24) * mm});
            skLineSegment(sketch, "E133", {"start": v(21.49, 24.5) * mm, "end": v(18.53, 24.5) * mm});
            skLineSegment(sketch, "E134", {"start": v(16.31, 24) * mm, "end": v(14.4, 24) * mm});
            skLineSegment(sketch, "E135", {"start": v(16.31, 24.5) * mm, "end": v(14.4, 24.5) * mm});
            skLineSegment(sketch, "E136", {"start": v(12.18, 24) * mm, "end": v(10.28, 24) * mm});
            skLineSegment(sketch, "E137", {"start": v(12.18, 24.5) * mm, "end": v(10.28, 24.5) * mm});
            skLineSegment(sketch, "E138", {"start": v(8.05, 24) * mm, "end": v(6.15, 24) * mm});
            skLineSegment(sketch, "E139", {"start": v(8.05, 24.5) * mm, "end": v(6.15, 24.5) * mm});
            skLineSegment(sketch, "E140.0", {"start": v(3.93, 24.5) * mm, "end": v(3.93, 24) * mm});
            skLineSegment(sketch, "E141", {"start": v(1.47, 24) * mm, "end": v(3.93, 24) * mm});
            skLineSegment(sketch, "E142", {"start": v(0.97, 24.5) * mm, "end": v(3.93, 24.5) * mm});
            skLineSegment(sketch, "E143", {"start": v(0.97, 0.5) * mm, "end": v(0.97, 24.5) * mm});
            skLineSegment(sketch, "E144.0", {"start": v(3.93, 1) * mm, "end": v(3.93, 0.5) * mm});
            skLineSegment(sketch, "E145", {"start": v(1.47, 1) * mm, "end": v(3.93, 1) * mm});
            skLineSegment(sketch, "E146", {"start": v(0.97, 0.5) * mm, "end": v(3.93, 0.5) * mm});
            skLineSegment(sketch, "E147", {"start": v(6.15, 0.5) * mm, "end": v(8.24, 0.5) * mm});
            skLineSegment(sketch, "E148", {"start": v(6.15, 1) * mm, "end": v(8.24, 1) * mm});
            skLineSegment(sketch, "E149", {"start": v(10.28, 0.5) * mm, "end": v(12.05, 0.5) * mm});
            skLineSegment(sketch, "E150", {"start": v(10.28, 1) * mm, "end": v(12.05, 1) * mm});
            skLineSegment(sketch, "E151", {"start": v(14.4, 0.5) * mm, "end": v(16.31, 0.5) * mm});
            skLineSegment(sketch, "E152", {"start": v(14.4, 1) * mm, "end": v(16.31, 1) * mm});
            skSolve(sketch);
        }
        {
            var Q0;
            Q0 = qSketchRegion(id + "F36", true);
            extrude(context, id + "F37", {"entities" : qUnion([Q0]), "operationType" : NewBodyOperationType.REMOVE, "oppositeDirection" : true, "depth" : 0.5 * mm, "offsetDistance" : 25 * mm});
        }
        {
            var Q0;
            Q0=makeQuery(id+"F5.boolean.opBoolean","MERGE",FACE,{"derivedFrom":[makeQuery(id+"F1.opExtrude","CAP_FACE",FACE,{"disambiguationData":[OSD([sQuery(id+"F0.wireOp",EDGE,"E0"),sQuery(id+"F0.wireOp",EDGE,"E1"),sQuery(id+"F0.wireOp",EDGE,"E2"),sQuery(id+"F0.wireOp",EDGE,"E3"),sQuery(id+"F0.wireOp",EDGE,"E4"),sQuery(id+"F0.wireOp",EDGE,"E5"),sQuery(id+"F0.wireOp",EDGE,"E6"),sQuery(id+"F0.wireOp",EDGE,"E7"),sQuery(id+"F0.wireOp",EDGE,"E8"),sQuery(id+"F0.wireOp",EDGE,"E9"),sQuery(id+"F0.wireOp",EDGE,"E10"),sQuery(id+"F0.wireOp",EDGE,"E11"),sQuery(id+"F0.wireOp",EDGE,"E12"),sQuery(id+"F0.wireOp",EDGE,"E13"),sQuery(id+"F0.wireOp",EDGE,"E14"),sQuery(id+"F0.wireOp",EDGE,"E15"),sQuery(id+"F0.wireOp",EDGE,"E16"),sQuery(id+"F0.wireOp",EDGE,"E17"),sQuery(id+"F0.wireOp",EDGE,"E18"),sQuery(id+"F0.wireOp",EDGE,"E20.MirrorCS"),sQuery(id+"F0.wireOp",EDGE,"E21.MirrorCS"),sQuery(id+"F0.wireOp",EDGE,"E22.MirrorCS"),sQuery(id+"F0.wireOp",EDGE,"E23.MirrorCS"),sQuery(id+"F0.wireOp",EDGE,"E24.MirrorCS"),sQuery(id+"F0.wireOp",EDGE,"E25.MirrorCS"),sQuery(id+"F0.wireOp",EDGE,"E26.MirrorCS"),sQuery(id+"F0.wireOp",EDGE,"E27.MirrorCS"),sQuery(id+"F0.wireOp",EDGE,"E28.MirrorCS"),sQuery(id+"F0.wireOp",EDGE,"E29.MirrorCS"),sQuery(id+"F0.wireOp",EDGE,"E30.MirrorCS"),sQuery(id+"F0.wireOp",EDGE,"E31.MirrorCS"),sQuery(id+"F0.wireOp",EDGE,"E32.MirrorCS"),sQuery(id+"F0.wireOp",EDGE,"E33.MirrorCS"),sQuery(id+"F0.wireOp",EDGE,"E34.MirrorCS"),sQuery(id+"F0.wireOp",EDGE,"E35.MirrorCS"),sQuery(id+"F0.wireOp",EDGE,"E36.MirrorCS")])],"isStart":false}),makeQuery(id+"F5.opExtrude","SWEPT_FACE",FACE,{"disambiguationData":[OSD([sQuery(id+"F4.wireOp",EDGE,"E44")])]}),makeQuery(id+"F5.opExtrude","SWEPT_FACE",FACE,{"disambiguationData":[OSD([sQuery(id+"F4.wireOp",EDGE,"E49.trimOffspring")])]})]});
            var sketch = newSketch(context, id + "F38", { "sketchPlane" : qUnion([Q0])});
            skLineSegment(sketch, "E153.0", {"start": v(-21.75, 25) * mm, "end": v(-18.99, 25) * mm});
            skLineSegment(sketch, "E154.0", {"start": v(-18.99, 25) * mm, "end": v(-17.92, 27.28) * mm});
            skLineSegment(sketch, "E155.0", {"start": v(-17.92, 27.28) * mm, "end": v(-16.92, 27.28) * mm});
            skLineSegment(sketch, "E156.0", {"start": v(-16.92, 27.28) * mm, "end": v(-15.86, 25) * mm});
            skLineSegment(sketch, "E157.0", {"start": v(-15.86, 25) * mm, "end": v(-14.86, 25) * mm});
            skLineSegment(sketch, "E158.0", {"start": v(-14.86, 25) * mm, "end": v(-13.8, 27.28) * mm});
            skLineSegment(sketch, "E159.0", {"start": v(-13.8, 27.28) * mm, "end": v(-12.8, 27.28) * mm});
            skLineSegment(sketch, "E160.0", {"start": v(-12.8, 27.28) * mm, "end": v(-11.73, 25) * mm});
            skLineSegment(sketch, "E161.0", {"start": v(-11.73, 25) * mm, "end": v(-10.73, 25) * mm});
            skLineSegment(sketch, "E162.0", {"start": v(-10.73, 25) * mm, "end": v(-9.67, 27.28) * mm});
            skLineSegment(sketch, "E163.0", {"start": v(-9.67, 27.28) * mm, "end": v(-8.67, 27.28) * mm});
            skLineSegment(sketch, "E164.0", {"start": v(-8.67, 27.28) * mm, "end": v(-7.6, 25) * mm});
            skLineSegment(sketch, "E165.0", {"start": v(-7.6, 25) * mm, "end": v(-6.6, 25) * mm});
            skLineSegment(sketch, "E166.0", {"start": v(-6.6, 25) * mm, "end": v(-5.54, 27.28) * mm});
            skLineSegment(sketch, "E167.0", {"start": v(-5.54, 27.28) * mm, "end": v(-4.54, 27.28) * mm});
            skLineSegment(sketch, "E168.0", {"start": v(-4.54, 27.28) * mm, "end": v(-3.47, 25) * mm});
            skLineSegment(sketch, "E169.0", {"start": v(-3.47, 25) * mm, "end": v(-0.7, 25) * mm});
            skArc(sketch, "E170.0", {"start": v(1.53, 24) * mm, "mid": v(0.52, 24.74) * mm, "end": v(-0.7, 25) * mm});
            skLineSegment(sketch, "E171", {"start": v(-11.23, 25) * mm, "end": v(-11.23, 16.3) * mm, "construction": true});
            skLineSegment(sketch, "E172.0", {"start": v(1.38, 23.85) * mm, "end": v(1.53, 24) * mm});
            skLineSegment(sketch, "E173", {"start": v(0.67, 23.85) * mm, "end": v(1.34, 23.32) * mm});
            skLineSegment(sketch, "E174", {"start": v(1.34, 23.32) * mm, "end": v(1.84, 23.95) * mm});
            skLineSegment(sketch, "E175", {"start": v(1.84, 23.95) * mm, "end": v(1.84, 28) * mm});
            skPoint(sketch, "E176.orphan", {"position": v(0.67, 23.15) * mm});
            skLineSegment(sketch, "E177.MirrorCS", {"start": v(-23.84, 23.85) * mm, "end": v(-23.99, 24) * mm});
            skLineSegment(sketch, "E178.MirrorCS", {"start": v(-23.8, 23.32) * mm, "end": v(-24.3, 23.95) * mm});
            skLineSegment(sketch, "E179.MirrorCS", {"start": v(-23.13, 23.85) * mm, "end": v(-23.8, 23.32) * mm});
            skPoint(sketch, "E180.MirrorP", {"position": v(-23.13, 23.15) * mm});
            skArc(sketch, "E181.MirrorCS", {"start": v(-23.99, 24) * mm, "mid": v(-22.98, 24.74) * mm, "end": v(-21.75, 25) * mm});
            skLineSegment(sketch, "E182.MirrorCS", {"start": v(-24.3, 23.95) * mm, "end": v(-24.3, 28) * mm});
            skLineSegment(sketch, "E183", {"start": v(-24.3, 28) * mm, "end": v(1.84, 28) * mm});
            skSolve(sketch);
        }
        {
            var Q0;
            Q0=makeQuery(id+"F38.imprint","IMPRINT",FACE,{"disambiguationData":[TD([[makeQuery(id+"F38.imprint","IMPRINT",EDGE,{"derivedFrom":sQuery(id+"F38.wireOp",EDGE,"E153.0")}),1.0]])]});
            extrude(context, id + "F39", {"entities" : qUnion([Q0]), "oppositeDirection" : true, "depth" : 25 * mm, "offsetDistance" : 25 * mm});
        }
        {
            var Q0;
            Q0=makeQuery(id+"F39.opExtrude","SWEPT_EDGE",EDGE,{"disambiguationData":[OSD([sQuery(id+"F38.wireOp",EDGE,"E175"),sQuery(id+"F38.wireOp",EDGE,"E183")])]});
            var Q1;
            Q1=makeQuery(id+"F39.opExtrude","SWEPT_EDGE",EDGE,{"disambiguationData":[OSD([sQuery(id+"F38.wireOp",EDGE,"E182.MirrorCS"),sQuery(id+"F38.wireOp",EDGE,"E183")])]});
            fillet(context, id + "F40", {"entities" : qUnion([Q0, Q1]), "radius" : 5 * mm, "tangentPropagation" : true, "allowEdgeOverflow" : false});
        }
        {
            var Q0;
            Q0=makeQuery(id+"F39.opExtrude","SWEPT_EDGE",EDGE,{"disambiguationData":[OSD([sQuery(id+"F38.wireOp",EDGE,"E173"),sQuery(id+"F38.wireOp",EDGE,"E174")])]});
            var Q1;
            Q1=makeQuery(id+"F40.opFillet","BLEND_EDGE",EDGE,{"blendedFrom":[makeQuery(id+"F39.opExtrude","SWEPT_EDGE",EDGE,{"disambiguationData":[OSD([sQuery(id+"F38.wireOp",EDGE,"E175"),sQuery(id+"F38.wireOp",EDGE,"E183")])]}),makeQuery(id+"F39.opExtrude","SWEPT_FACE",FACE,{"disambiguationData":[OSD([sQuery(id+"F38.wireOp",EDGE,"E174")])]})],"blendedInto":[makeQuery(id+"F39.opExtrude","SWEPT_FACE",FACE,{"disambiguationData":[OSD([sQuery(id+"F38.wireOp",EDGE,"E174")])]})]});
            var Q2;
            Q2=makeQuery(id+"F40.opFillet","BLEND_EDGE",EDGE,{"blendedFrom":[makeQuery(id+"F39.opExtrude","SWEPT_EDGE",EDGE,{"disambiguationData":[OSD([sQuery(id+"F38.wireOp",EDGE,"E182.MirrorCS"),sQuery(id+"F38.wireOp",EDGE,"E183")])]}),makeQuery(id+"F39.opExtrude","SWEPT_FACE",FACE,{"disambiguationData":[OSD([sQuery(id+"F38.wireOp",EDGE,"E178.MirrorCS")])]})],"blendedInto":[makeQuery(id+"F39.opExtrude","SWEPT_FACE",FACE,{"disambiguationData":[OSD([sQuery(id+"F38.wireOp",EDGE,"E178.MirrorCS")])]})]});
            var Q3;
            Q3=makeQuery(id+"F39.opExtrude","SWEPT_EDGE",EDGE,{"disambiguationData":[OSD([sQuery(id+"F38.wireOp",EDGE,"E178.MirrorCS"),sQuery(id+"F38.wireOp",EDGE,"E179.MirrorCS")])]});
            fillet(context, id + "F41", {"entities" : qUnion([Q0, Q1, Q2, Q3]), "radius" : 0.5 * mm, "tangentPropagation" : true, "allowEdgeOverflow" : false});
        }
        {
            var Q0;
            Q0=makeQuery(id+"F1.opExtrude","SWEPT_FACE",FACE,{"disambiguationData":[OSD([sQuery(id+"F0.wireOp",EDGE,"E18")])]});
            var sketch = newSketch(context, id + "F42", { "sketchPlane" : qUnion([Q0])});
            skLineSegment(sketch, "E184.bottom", {"start": v(14.53, 16.07) * mm, "end": v(11.7, 16.07) * mm});
            skLineSegment(sketch, "E184.top", {"start": v(14.53, 8.77) * mm, "end": v(11.7, 8.77) * mm});
            skLineSegment(sketch, "E184.left", {"start": v(14.53, 16.07) * mm, "end": v(14.53, 8.77) * mm});
            skLineSegment(sketch, "E184.right", {"start": v(11.7, 16.07) * mm, "end": v(11.7, 8.77) * mm});
            skSolve(sketch);
        }
        {
            var Q0;
            Q0=makeQuery(id+"F42.imprint","IMPRINT",FACE,{"disambiguationData":[TD([[makeQuery(id+"F42.imprint","IMPRINT",EDGE,{"derivedFrom":sQuery(id+"F42.wireOp",EDGE,"E184.bottom")}),1.0]])]});
            extrude(context, id + "F43", {"entities" : qUnion([Q0]), "operationType" : NewBodyOperationType.ADD, "depth" : 3 * mm, "offsetDistance" : 25 * mm});
        }
        {
            var Q0;
            Q0=makeQuery(id+"F43.opExtrude","SWEPT_FACE",FACE,{"disambiguationData":[OSD([sQuery(id+"F42.wireOp",EDGE,"E184.left")])]});
            var sketch = newSketch(context, id + "F44", { "sketchPlane" : qUnion([Q0])});
            skLineSegment(sketch, "E185.bottom", {"start": v(-0.34, 9.56) * mm, "end": v(-1.71, 9.56) * mm});
            skLineSegment(sketch, "E185.top", {"start": v(-0.34, 15.33) * mm, "end": v(-1.71, 15.33) * mm});
            skLineSegment(sketch, "E185.left", {"start": v(-0.34, 9.56) * mm, "end": v(-0.34, 15.33) * mm});
            skLineSegment(sketch, "E185.right", {"start": v(-1.71, 9.56) * mm, "end": v(-1.71, 15.33) * mm});
            skSolve(sketch);
        }
        {
            var Q0;
            Q0=makeQuery(id+"F44.imprint","IMPRINT",FACE,{"disambiguationData":[TD([[makeQuery(id+"F44.imprint","IMPRINT",EDGE,{"derivedFrom":sQuery(id+"F44.wireOp",EDGE,"E185.bottom")}),-1.0]])]});
            extrude(context, id + "F45", {"entities" : qUnion([Q0]), "operationType" : NewBodyOperationType.REMOVE, "oppositeDirection" : true, "depth" : 20 * mm, "offsetDistance" : 25 * mm});
        }
        {
            var Q0;
            Q0=makeQuery(id+"F43.opExtrude","CAP_EDGE",EDGE,{"disambiguationData":[OSD([sQuery(id+"F42.wireOp",EDGE,"E184.top")])],"isStart":false});
            var Q1;
            Q1=makeQuery(id+"F43.opExtrude","CAP_EDGE",EDGE,{"disambiguationData":[OSD([sQuery(id+"F42.wireOp",EDGE,"E184.bottom")])],"isStart":false});
            fillet(context, id + "F46", {"entities" : qUnion([Q0, Q1]), "radius" : 2 * mm, "tangentPropagation" : true, "allowEdgeOverflow" : false});
        }
        {
            var Q0;
            Q0=makeQuery(id+"F45.boolean.opBoolean","COPY",EDGE,{"derivedFrom":makeQuery(id+"F45.opExtrude","SWEPT_EDGE",EDGE,{"disambiguationData":[OSD([sQuery(id+"F44.wireOp",EDGE,"E185.top"),sQuery(id+"F44.wireOp",EDGE,"E185.right")])]})});
            var Q1;
            Q1=makeQuery(id+"F45.boolean.opBoolean","COPY",EDGE,{"derivedFrom":makeQuery(id+"F45.opExtrude","SWEPT_EDGE",EDGE,{"disambiguationData":[OSD([sQuery(id+"F44.wireOp",EDGE,"E185.bottom"),sQuery(id+"F44.wireOp",EDGE,"E185.right")])]})});
            fillet(context, id + "F47", {"entities" : qUnion([Q0, Q1]), "radius" : 1 * mm, "tangentPropagation" : true, "allowEdgeOverflow" : false});
        }
        {
            var Q0;
            Q0=makeQuery(id+"F1.opExtrude","SWEPT_EDGE",EDGE,{"disambiguationData":[OSD([sQuery(id+"F0.wireOp",EDGE,"E18"),sQuery(id+"F0.wireOp",EDGE,"E31.MirrorCS")])]});
            var Q1;
            Q1=makeQuery(id+"F1.opExtrude","SWEPT_EDGE",EDGE,{"disambiguationData":[OSD([sQuery(id+"F0.wireOp",EDGE,"E0"),sQuery(id+"F0.wireOp",EDGE,"E25.MirrorCS")])]});
            fillet(context, id + "F48", {"entities" : qUnion([Q0, Q1]), "radius" : 3 * mm, "tangentPropagation" : true, "allowEdgeOverflow" : false});
        }
    });
